# Revit family: QF_Vollrath_PSG4-DG-208240-C_DOUBLE GROOVED PANINI SANDWICH GRILL
name_source: partatom
category: Generic Models
units: mm (PartAtom-declared; Revit-internal decimal feet)

## family parameters
Always vertical = No
Can host rebar = No
Cut with Voids When Loaded = No
OmniClass Number = 23.40.40.00
OmniClass Title = Food Service Equipment and Furnishings
Part Type = Normal
Room Calculation Point = No
Round Connector Dimension = Use Diameter
Shared = Yes
Work Plane-Based = Yes

## types (1)
- QF_Vollrath_PSG4-DG-208240-C_DOUBLE GROOVED PANINI SANDWICH GRILL
    Apparent Power = 3600 VA
    Conn Conduit = No
    Conn Plug = NEMA 6-20P
    Cycle = 60 Hz
    Default Elevation = 0 "
    Description = DOUBLE GROOVED PANINI GRILL
    Elec Conn Connection Height = 0 "
    FL Amps = 15 A
    Foodservice Equipment Identifier = Yes
    Manufacturer = Vollrath
    Max Overcurrent Protection = 0 A
    Min Ckt Ampacity = 0 A
    Model = TS18002-C
    Phase = 1
    Volts = 240 V
    Watts = 3600 W
    Weight = 20162.51
    Weight in Pounds = 0
    代号 = “图样代号”
    共X张 = 1
    名称 = “图样名称”
    日期 = 2007,12,3
    第X张 = 1
    质量 = 20162.51

## geometry (parser evidence)
native form markers: Sweep x3
no freeform markers — native parametric forms only
